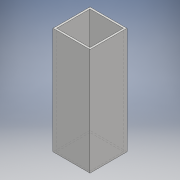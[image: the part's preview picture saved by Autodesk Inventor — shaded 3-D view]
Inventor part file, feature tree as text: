
AUTODESK INVENTOR PART (.ipt)
format: ipt  version: 2018 (Build 220112000, 112)  size: 96,256 bytes
history: native  units: mm
features: other x1, extrude x1, sketch x1
ambient origin geometry x8: Origin, YZ Plane, XZ Plane, XY Plane, X Axis, Y Axis, Z Axis, Center Point
bodies: Body1 (feature_tree)
feature tree (3):
  other  "ソリッド1"
  extrude  "押し出し1"  Depth=32.0mm
  sketch  "スケッチ1"
